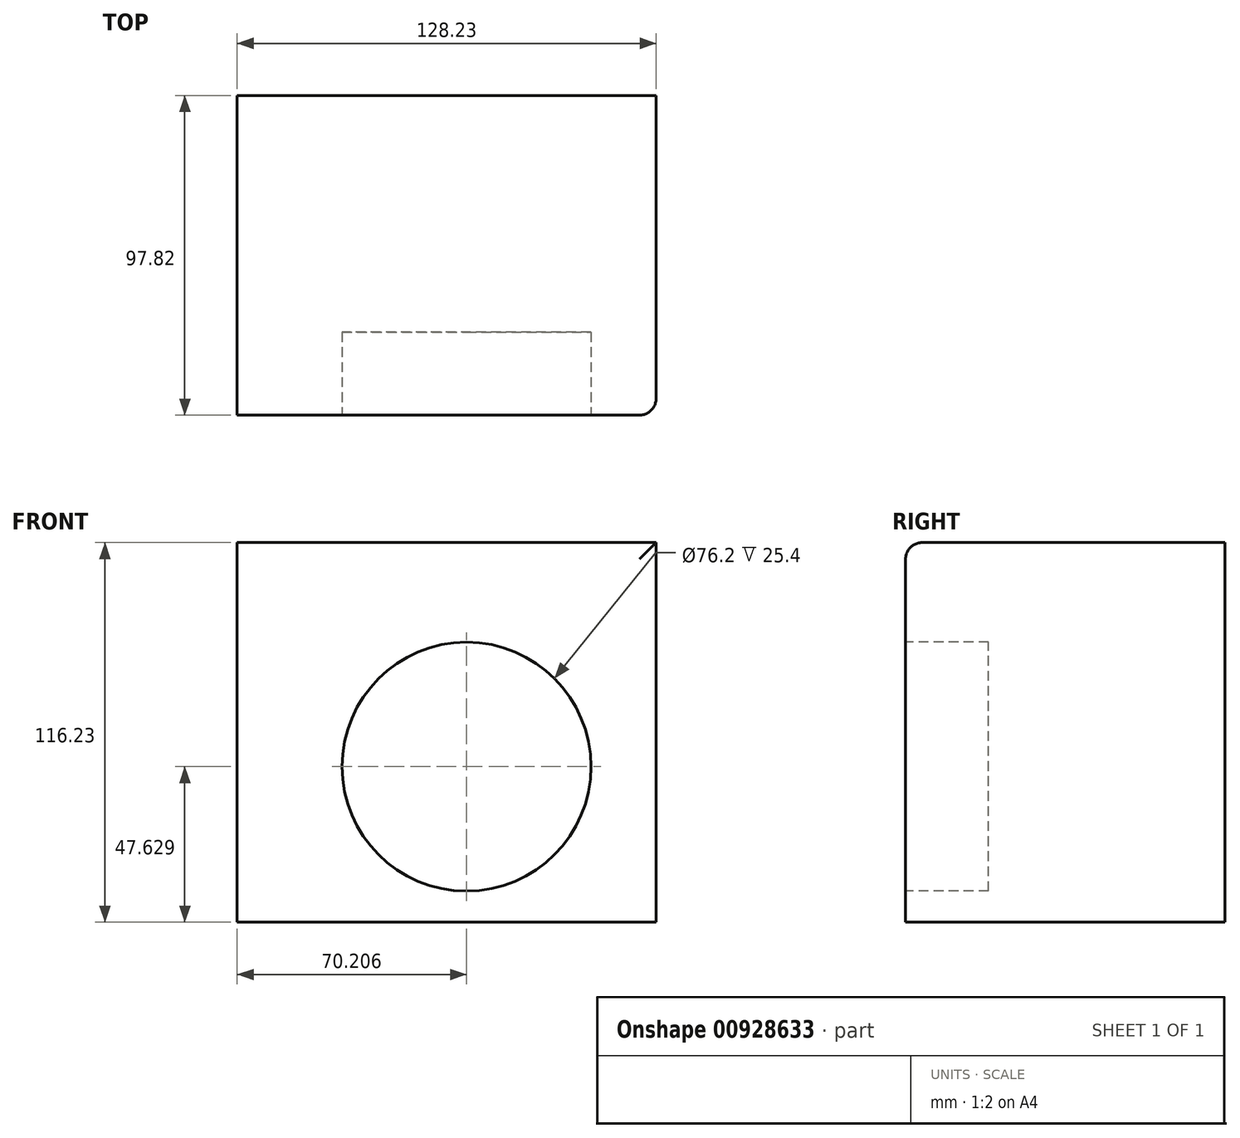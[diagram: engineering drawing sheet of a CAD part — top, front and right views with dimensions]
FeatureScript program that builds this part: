
annotation { "Feature Type Name" : "Feature", "Feature Type Description" : "" }
export const myFeature = defineFeature(function(context is Context, id is Id, definition is map)
    precondition{}
    {
        {
            var Q0;
            Q0=qCreatedBy(makeId("Top.planeOp"),FACE);
            var sketch = newSketch(context, id + "F0", { "sketchPlane" : qUnion([Q0])});
            skLineSegment(sketch, "E0.bottom", {"start": v(-56.65, -44.23) * mm, "end": v(71.58, -44.23) * mm});
            skLineSegment(sketch, "E0.top", {"start": v(-56.65, 53.59) * mm, "end": v(71.58, 53.59) * mm});
            skLineSegment(sketch, "E0.left", {"start": v(-56.65, -44.23) * mm, "end": v(-56.65, 53.59) * mm});
            skLineSegment(sketch, "E0.right", {"start": v(71.58, -44.23) * mm, "end": v(71.58, 53.59) * mm});
            skSolve(sketch);
        }
        {
            var Q0;
            Q0=makeQuery(id+"F0.imprint","IMPRINT",FACE,{"disambiguationData":[TD([[makeQuery(id+"F0.imprint","IMPRINT",EDGE,{"derivedFrom":sQuery(id+"F0.wireOp",EDGE,"E0.bottom")}),1.0]])]});
            extrude(context, id + "F1", {"entities" : qUnion([Q0]), "depth" : 116.23 * mm, "offsetDistance" : 25.4 * mm});
        }
        {
            var Q0;
            Q0=makeQuery(id+"F1.opExtrude","SWEPT_FACE",FACE,{"disambiguationData":[OSD([sQuery(id+"F0.wireOp",EDGE,"E0.bottom")])]});
            var sketch = newSketch(context, id + "F2", { "sketchPlane" : qUnion([Q0])});
            skCircle(sketch, "E1", {"center": v(13.56, 47.63) * mm, "radius": 38.1 * mm});
            skSolve(sketch);
        }
        {
            var Q0;
            Q0=makeQuery(id+"F2.imprint","IMPRINT",FACE,{"disambiguationData":[TD([[makeQuery(id+"F2.imprint","IMPRINT",EDGE,{"derivedFrom":sQuery(id+"F2.wireOp",EDGE,"E1")}),1.0]])]});
            extrude(context, id + "F3", {"entities" : qUnion([Q0]), "operationType" : NewBodyOperationType.REMOVE, "oppositeDirection" : true, "depth" : 25.4 * mm, "offsetDistance" : 25.4 * mm});
        }
        {
            var Q0;
            Q0=makeQuery(id+"F1.opExtrude","SWEPT_EDGE",EDGE,{"disambiguationData":[OSD([sQuery(id+"F0.wireOp",EDGE,"E0.bottom"),sQuery(id+"F0.wireOp",EDGE,"E0.right")])]});
            var Q1;
            Q1=makeQuery(id+"F1.opExtrude","CAP_EDGE",EDGE,{"disambiguationData":[OSD([sQuery(id+"F0.wireOp",EDGE,"E0.bottom")])],"isStart":false});
            var Q2;
            Q2=makeQuery(id+"F3.boolean.opBoolean","COPY",EDGE,{"derivedFrom":makeQuery(id+"F3.opExtrude","CAP_EDGE",EDGE,{"disambiguationData":[OSD([sQuery(id+"F2.wireOp",EDGE,"E1")])],"isStart":true})});
            fillet(context, id + "F4", {"entities" : qUnion([Q0, Q1, Q2]), "radius" : 5.08 * mm, "tangentPropagation" : true, "allowEdgeOverflow" : false});
        }
    });
